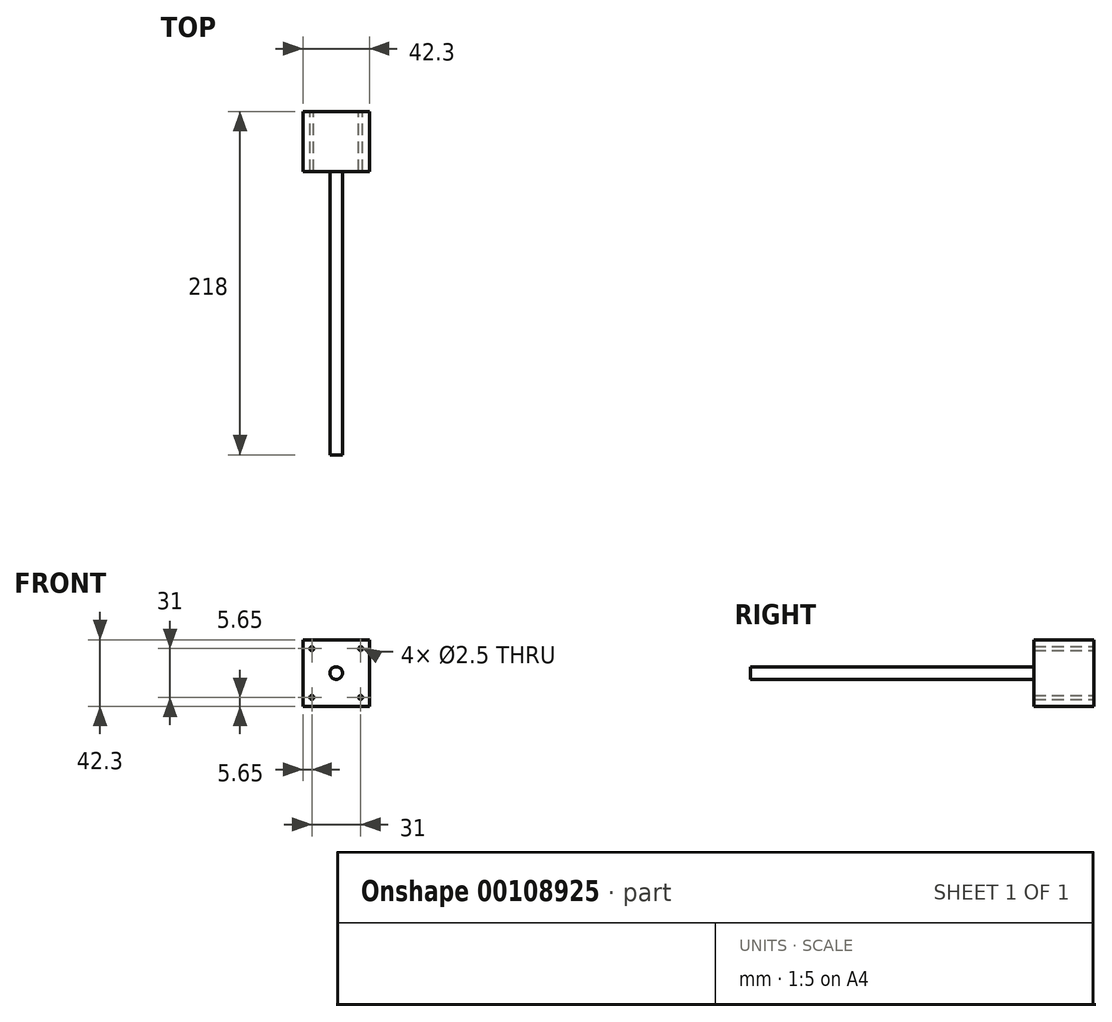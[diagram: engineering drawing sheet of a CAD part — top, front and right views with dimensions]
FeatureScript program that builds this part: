
annotation { "Feature Type Name" : "Feature", "Feature Type Description" : "" }
export const myFeature = defineFeature(function(context is Context, id is Id, definition is map)
    precondition{}
    {
        {
            var Q0;
            Q0=qCreatedBy(makeId("Front.planeOp"),FACE);
            var sketch = newSketch(context, id + "F0", { "sketchPlane" : qUnion([Q0])});
            skLineSegment(sketch, "E0.bottom", {"start": v(21.15, -21.15) * mm, "end": v(-21.15, -21.15) * mm});
            skLineSegment(sketch, "E0.top", {"start": v(21.15, 21.15) * mm, "end": v(-21.15, 21.15) * mm});
            skLineSegment(sketch, "E0.left", {"start": v(21.15, -21.15) * mm, "end": v(21.15, 21.15) * mm});
            skLineSegment(sketch, "E0.right", {"start": v(-21.15, -21.15) * mm, "end": v(-21.15, 21.15) * mm});
            skPoint(sketch, "E0.middle", {"position": v(0, 0) * mm});
            skLineSegment(sketch, "E1.bottom", {"start": v(15.5, 15.5) * mm, "end": v(-15.5, 15.5) * mm, "construction": true});
            skLineSegment(sketch, "E1.top", {"start": v(15.5, -15.5) * mm, "end": v(-15.5, -15.5) * mm, "construction": true});
            skLineSegment(sketch, "E1.left", {"start": v(15.5, 15.5) * mm, "end": v(15.5, -15.5) * mm, "construction": true});
            skLineSegment(sketch, "E1.right", {"start": v(-15.5, 15.5) * mm, "end": v(-15.5, -15.5) * mm, "construction": true});
            skPoint(sketch, "E2", {"position": v(-15.5, 15.5) * mm});
            skPoint(sketch, "E3", {"position": v(15.5, 15.5) * mm});
            skPoint(sketch, "E4", {"position": v(15.5, -15.5) * mm});
            skPoint(sketch, "E5", {"position": v(-15.5, -15.5) * mm});
            skCircle(sketch, "E6", {"center": v(-15.5, 15.5) * mm, "radius": 1.25 * mm});
            skCircle(sketch, "E7", {"center": v(15.5, 15.5) * mm, "radius": 1.25 * mm});
            skCircle(sketch, "E8", {"center": v(15.5, -15.5) * mm, "radius": 1.25 * mm});
            skCircle(sketch, "E9", {"center": v(-15.5, -15.5) * mm, "radius": 1.25 * mm});
            skSolve(sketch);
        }
        {
            var Q0;
            Q0 = qSketchRegion(id + "F0", true);
            extrude(context, id + "F1", {"entities" : qUnion([Q0]), "endBound" : BoundingType.SYMMETRIC, "depth" : 38 * mm});
        }
        {
            var Q0;
            Q0=makeQuery(id+"F1.opExtrude","CAP_FACE",FACE,{"disambiguationData":[OSD([sQuery(id+"F0.wireOp",EDGE,"E0.bottom"),sQuery(id+"F0.wireOp",EDGE,"E0.top"),sQuery(id+"F0.wireOp",EDGE,"E0.left"),sQuery(id+"F0.wireOp",EDGE,"E0.right"),sQuery(id+"F0.wireOp",EDGE,"E6"),sQuery(id+"F0.wireOp",EDGE,"E7"),sQuery(id+"F0.wireOp",EDGE,"E8"),sQuery(id+"F0.wireOp",EDGE,"E9")])],"isStart":false});
            var sketch = newSketch(context, id + "F2", { "sketchPlane" : qUnion([Q0])});
            skCircle(sketch, "E10", {"center": v(0, 0) * mm, "radius": 4 * mm});
            skSolve(sketch);
        }
        {
            var Q0;
            Q0 = qSketchRegion(id + "F2", true);
            extrude(context, id + "F3", {"entities" : qUnion([Q0]), "operationType" : NewBodyOperationType.ADD, "depth" : 180 * mm});
        }
    });
